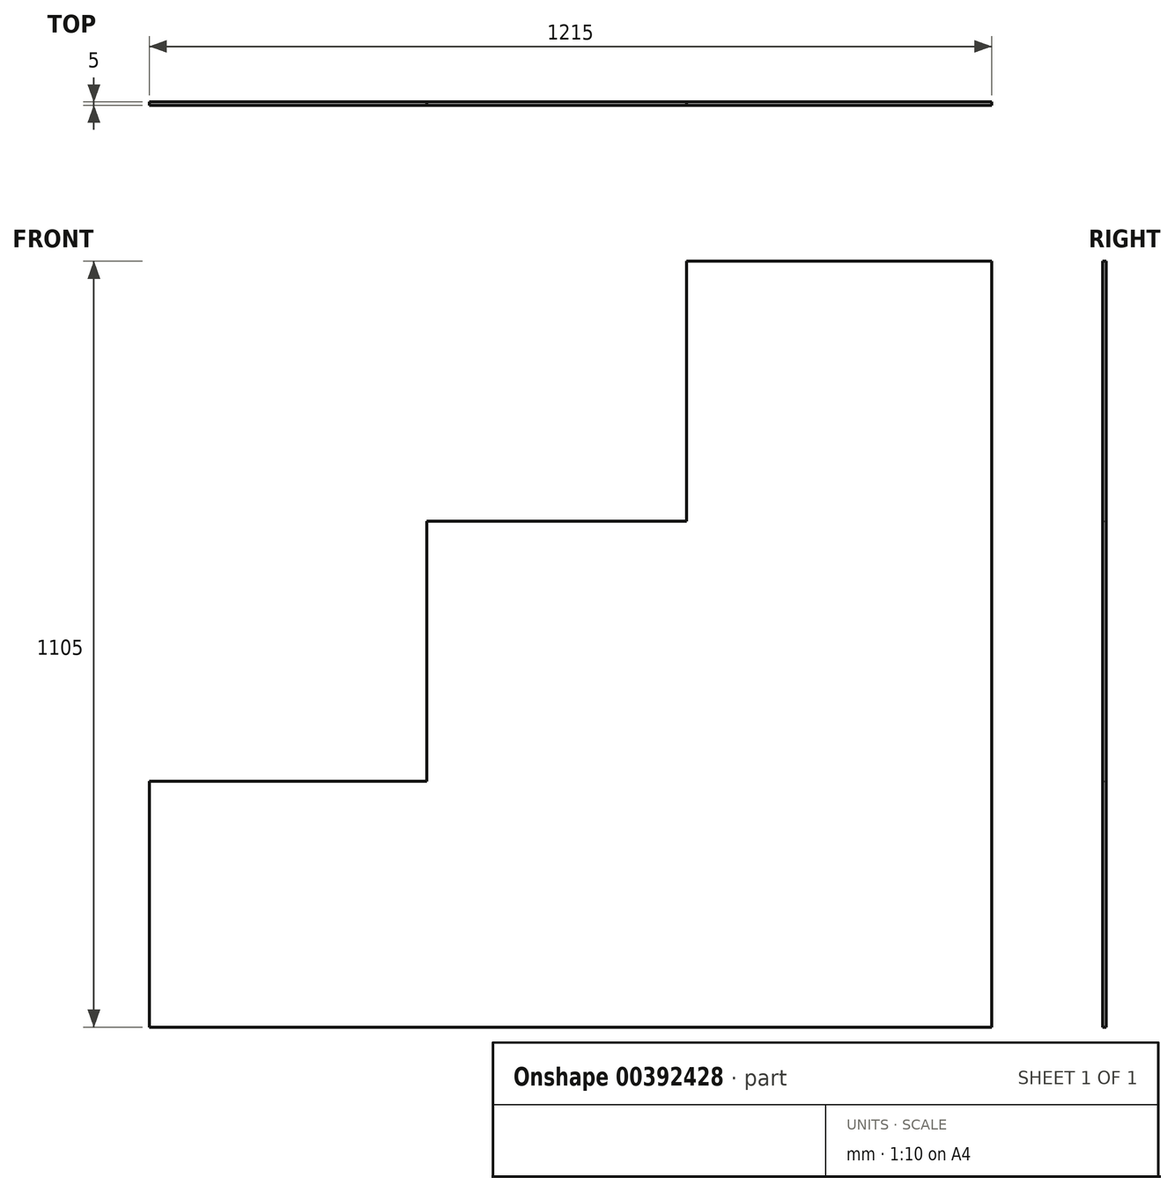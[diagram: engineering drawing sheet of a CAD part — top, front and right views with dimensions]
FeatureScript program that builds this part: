
annotation { "Feature Type Name" : "Feature", "Feature Type Description" : "" }
export const myFeature = defineFeature(function(context is Context, id is Id, definition is map)
    precondition{}
    {
        {
            var Q0;
            Q0=qCreatedBy(makeId("Front.planeOp"),FACE);
            var sketch = newSketch(context, id + "F0", { "sketchPlane" : qUnion([Q0])});
            skLineSegment(sketch, "E0.bottom", {"start": v(-1215, 0) * mm, "end": v(0, 0) * mm});
            skLineSegment(sketch, "E0.top", {"start": v(-1215, -355) * mm, "end": v(0, -355) * mm});
            skLineSegment(sketch, "E0.left", {"start": v(-1215, 0) * mm, "end": v(-1215, -355) * mm});
            skLineSegment(sketch, "E0.right", {"start": v(0, 0) * mm, "end": v(0, -355) * mm});
            skLineSegment(sketch, "E1.bottom", {"start": v(-815, 375) * mm, "end": v(0, 375) * mm});
            skLineSegment(sketch, "E1.top", {"start": v(-815, 20) * mm, "end": v(0, 20) * mm});
            skLineSegment(sketch, "E1.left", {"start": v(-815, 375) * mm, "end": v(-815, 20) * mm});
            skLineSegment(sketch, "E1.right", {"start": v(0, 375) * mm, "end": v(0, 20) * mm});
            skLineSegment(sketch, "E2.bottom", {"start": v(-440, 750) * mm, "end": v(0, 750) * mm});
            skLineSegment(sketch, "E2.top", {"start": v(-440, 395) * mm, "end": v(0, 395) * mm});
            skLineSegment(sketch, "E2.left", {"start": v(-440, 750) * mm, "end": v(-440, 395) * mm});
            skLineSegment(sketch, "E2.right", {"start": v(0, 750) * mm, "end": v(0, 395) * mm});
            skLineSegment(sketch, "E3", {"start": v(0, 395) * mm, "end": v(0, 0) * mm});
            skLineSegment(sketch, "E4", {"start": v(-440, 395) * mm, "end": v(-440, 0) * mm});
            skLineSegment(sketch, "E5", {"start": v(-815, 20) * mm, "end": v(-815, 0) * mm});
            skSolve(sketch);
        }
        {
            var Q0;
            Q0=makeQuery(id+"F0.imprint","IMPRINT",FACE,{"disambiguationData":[TD([[makeQuery(id+"F0.imprint","IMPRINT",EDGE,{"derivedFrom":sQuery(id+"F0.wireOp",EDGE,"E0.bottom")}),-1.0]])]});
            var Q1;
            Q1=makeQuery(id+"F0.imprint","IMPRINT",FACE,{"disambiguationData":[TD([[makeQuery(id+"F0.imprint","IMPRINT",EDGE,{"derivedFrom":sQuery(id+"F0.wireOp",EDGE,"E1.bottom")}),-1.0]])]});
            var Q2;
            Q2=makeQuery(id+"F0.imprint","IMPRINT",FACE,{"disambiguationData":[TD([[makeQuery(id+"F0.imprint","IMPRINT",EDGE,{"derivedFrom":sQuery(id+"F0.wireOp",EDGE,"E2.bottom")}),-1.0]])]});
            var Q3;
            {var subQ5=sQuery(id+"F0.wireOp",EDGE,"E2.top");Q3=makeQuery(id+"F0.imprint","IMPRINT",FACE,{"disambiguationData":[TD([[makeQuery(id+"F0.imprint","IMPRINT",EDGE,{"derivedFrom":subQ5}),-1.0]])]});}
            var Q4;
            {var subQ0=sQuery(id+"F0.wireOp",EDGE,"E3");var subQ5=sQuery(id+"F0.wireOp",EDGE,"E1.top");var subQ6=makeQuery(id+"F0.imprint","INTERSECT",VERTEX,{"derivedFrom":[subQ5,subQ0]});Q4=makeQuery(id+"F0.imprint","IMPRINT",FACE,{"disambiguationData":[TD([[makeQuery(id+"F0.imprint","IMPRINT",EDGE,{"disambiguationData":[TD([[subQ6,1.0]])],"derivedFrom":subQ5}),-1.0]])]});}
            var Q5;
            {var subQ3=sQuery(id+"F0.wireOp",EDGE,"E5");Q5=makeQuery(id+"F0.imprint","IMPRINT",FACE,{"disambiguationData":[TD([[makeQuery(id+"F0.imprint","IMPRINT",EDGE,{"derivedFrom":subQ3}),1.0]])]});}
            extrude(context, id + "F1", {"entities" : qUnion([Q0, Q1, Q2, Q3, Q4, Q5]), "depth" : 5 * mm});
        }
    });
